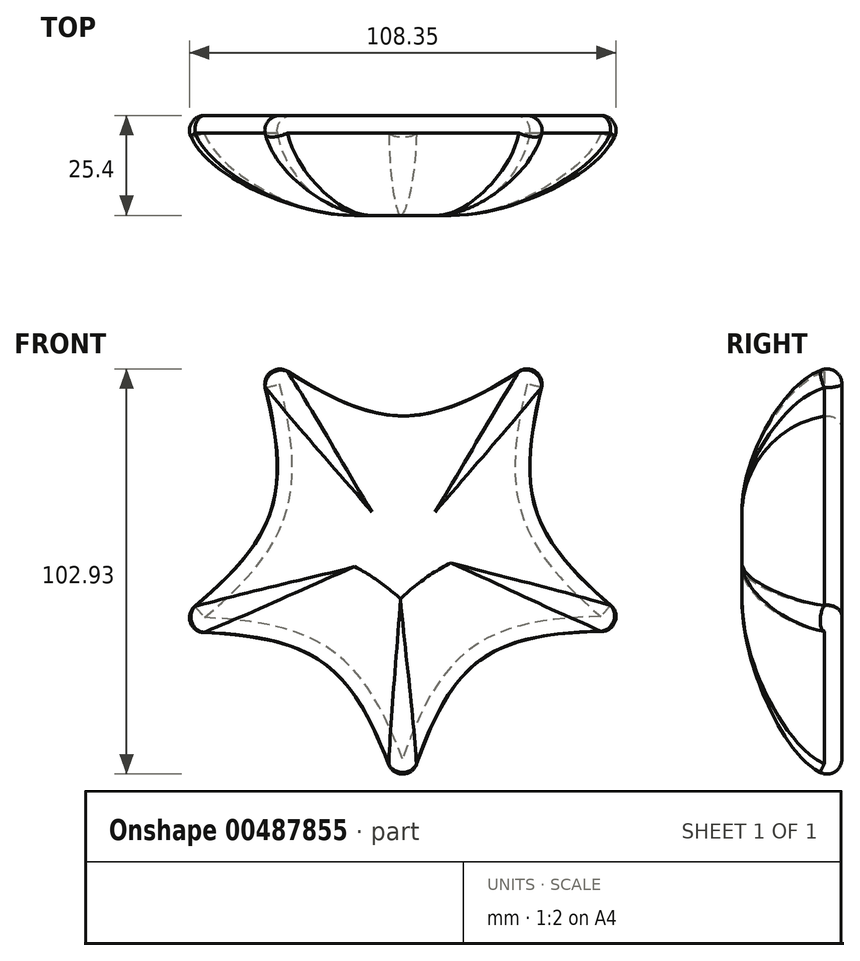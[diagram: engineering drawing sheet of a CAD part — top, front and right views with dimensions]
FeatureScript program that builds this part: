
annotation { "Feature Type Name" : "Feature", "Feature Type Description" : "" }
export const myFeature = defineFeature(function(context is Context, id is Id, definition is map)
    precondition{}
    {
        {
            var Q0;
            Q0=qCreatedBy(makeId("Front.planeOp"),FACE);
            var sketch = newSketch(context, id + "F0", { "sketchPlane" : qUnion([Q0])});
            skPoint(sketch, "E0.0.midPoint", {"position": v(0, 52.63) * mm});
            skFitSpline(sketch, "E1", {"points": [v(-38.24, 52.63) * mm, v(-33.94, 11.03) * mm, v(-61.87, -20.1) * mm], "startDerivative": vector(24.7, -88.44) * mm, "endDerivative": vector(-71.96, -57.03) * mm});
            skFitSpline(sketch, "E2", {"points": [v(-61.87, -20.1) * mm, v(-20.4, -28.09) * mm, v(0, -65.05) * mm], "startDerivative": vector(93.45, -1.48) * mm, "endDerivative": vector(30.29, -88.42) * mm});
            skFitSpline(sketch, "E3", {"points": [v(0, -65.05) * mm, v(19.82, -27.28) * mm, v(61.87, -20.1) * mm], "startDerivative": vector(28.53, 90.84) * mm, "endDerivative": vector(95.21, -0.94) * mm});
            skFitSpline(sketch, "E4", {"points": [v(61.87, -20.1) * mm, v(34.13, 11.1) * mm, v(38.24, 52.63) * mm], "startDerivative": vector(-71.4, 57.21) * mm, "endDerivative": vector(24.14, 88.25) * mm});
            skFitSpline(sketch, "E5", {"points": [v(38.24, 52.63) * mm, v(0, 35.4) * mm, v(-38.24, 52.63) * mm], "startDerivative": vector(-76.48, -51.72) * mm, "endDerivative": vector(-76.48, 51.72) * mm});
            skSolve(sketch);
        }
        {
            var Q0;
            Q0=makeQuery(id+"F0.imprint","IMPRINT",FACE,{"disambiguationData":[TD([[makeQuery(id+"F0.imprint","IMPRINT",EDGE,{"derivedFrom":sQuery(id+"F0.wireOp",EDGE,"E1")}),1.0]])]});
            extrude(context, id + "F1", {"entities" : qUnion([Q0]), "depth" : 25.4 * mm});
        }
        {
            var Q0;
            Q0=makeQuery(id+"F1.opExtrude","CAP_FACE",FACE,{"disambiguationData":[OSD([sQuery(id+"F0.wireOp",EDGE,"E1"),sQuery(id+"F0.wireOp",EDGE,"E2"),sQuery(id+"F0.wireOp",EDGE,"E3"),sQuery(id+"F0.wireOp",EDGE,"E4"),sQuery(id+"F0.wireOp",EDGE,"E5")])],"isStart":false});
            fillet(context, id + "F2", {"entities" : qUnion([Q0]), "radius" : 25.4 * mm, "tangentPropagation" : true, "allowEdgeOverflow" : false});
        }
        {
            var Q0;
            Q0=makeQuery(id+"F2.opFillet","BLEND_EDGE",EDGE,{"blendedFrom":[makeQuery(id+"F1.opExtrude","CAP_EDGE",EDGE,{"disambiguationData":[OSD([sQuery(id+"F0.wireOp",EDGE,"E1")])],"isStart":false}),makeQuery(id+"F1.opExtrude","CAP_EDGE",EDGE,{"disambiguationData":[OSD([sQuery(id+"F0.wireOp",EDGE,"E5")])],"isStart":false})],"blendedInto":[]});
            var Q1;
            {var subQ0=sQuery(id+"F0.wireOp",EDGE,"E4");Q1=makeQuery(id+"F2.opFillet","BLEND_EDGE",EDGE,{"blendedFrom":[makeQuery(id+"F1.opExtrude","CAP_EDGE",EDGE,{"disambiguationData":[OSD([subQ0])],"isStart":false}),makeQuery(id+"F1.opExtrude","CAP_FACE",FACE,{"disambiguationData":[OSD([sQuery(id+"F0.wireOp",EDGE,"E1"),sQuery(id+"F0.wireOp",EDGE,"E2"),sQuery(id+"F0.wireOp",EDGE,"E3"),subQ0,sQuery(id+"F0.wireOp",EDGE,"E5")])],"isStart":true})],"blendedInto":[makeQuery(id+"F1.opExtrude","CAP_FACE",FACE,{"disambiguationData":[OSD([sQuery(id+"F0.wireOp",EDGE,"E1"),sQuery(id+"F0.wireOp",EDGE,"E2"),sQuery(id+"F0.wireOp",EDGE,"E3"),subQ0,sQuery(id+"F0.wireOp",EDGE,"E5")])],"isStart":true})]});}
            fillet(context, id + "F3", {"entities" : qUnion([Q0, Q1]), "radius" : 3.8 * mm, "tangentPropagation" : true, "allowEdgeOverflow" : false});
        }
        {
            var Q0;
            Q0=makeQuery(id+"F2.opFillet","BLEND_EDGE",EDGE,{"blendedFrom":[makeQuery(id+"F1.opExtrude","CAP_EDGE",EDGE,{"disambiguationData":[OSD([sQuery(id+"F0.wireOp",EDGE,"E4")])],"isStart":false}),makeQuery(id+"F1.opExtrude","CAP_EDGE",EDGE,{"disambiguationData":[OSD([sQuery(id+"F0.wireOp",EDGE,"E5")])],"isStart":false})],"blendedInto":[]});
            fillet(context, id + "F4", {"entities" : qUnion([Q0]), "radius" : 3.8 * mm, "tangentPropagation" : true, "allowEdgeOverflow" : false});
        }
        {
            var Q0;
            Q0=makeQuery(id+"F2.opFillet","BLEND_EDGE",EDGE,{"blendedFrom":[makeQuery(id+"F1.opExtrude","CAP_EDGE",EDGE,{"disambiguationData":[OSD([sQuery(id+"F0.wireOp",EDGE,"E2")])],"isStart":false}),makeQuery(id+"F1.opExtrude","CAP_EDGE",EDGE,{"disambiguationData":[OSD([sQuery(id+"F0.wireOp",EDGE,"E3")])],"isStart":false})],"blendedInto":[]});
            var Q1;
            Q1=makeQuery(id+"F2.opFillet","BLEND_EDGE",EDGE,{"blendedFrom":[makeQuery(id+"F1.opExtrude","CAP_EDGE",EDGE,{"disambiguationData":[OSD([sQuery(id+"F0.wireOp",EDGE,"E3")])],"isStart":false}),makeQuery(id+"F1.opExtrude","CAP_EDGE",EDGE,{"disambiguationData":[OSD([sQuery(id+"F0.wireOp",EDGE,"E4")])],"isStart":false})],"blendedInto":[]});
            var Q2;
            Q2=makeQuery(id+"F2.opFillet","BLEND_EDGE",EDGE,{"blendedFrom":[makeQuery(id+"F1.opExtrude","CAP_EDGE",EDGE,{"disambiguationData":[OSD([sQuery(id+"F0.wireOp",EDGE,"E1")])],"isStart":false}),makeQuery(id+"F1.opExtrude","CAP_EDGE",EDGE,{"disambiguationData":[OSD([sQuery(id+"F0.wireOp",EDGE,"E2")])],"isStart":false})],"blendedInto":[]});
            fillet(context, id + "F5", {"entities" : qUnion([Q0, Q1, Q2]), "radius" : 3.8 * mm, "tangentPropagation" : true, "allowEdgeOverflow" : false});
        }
    });
